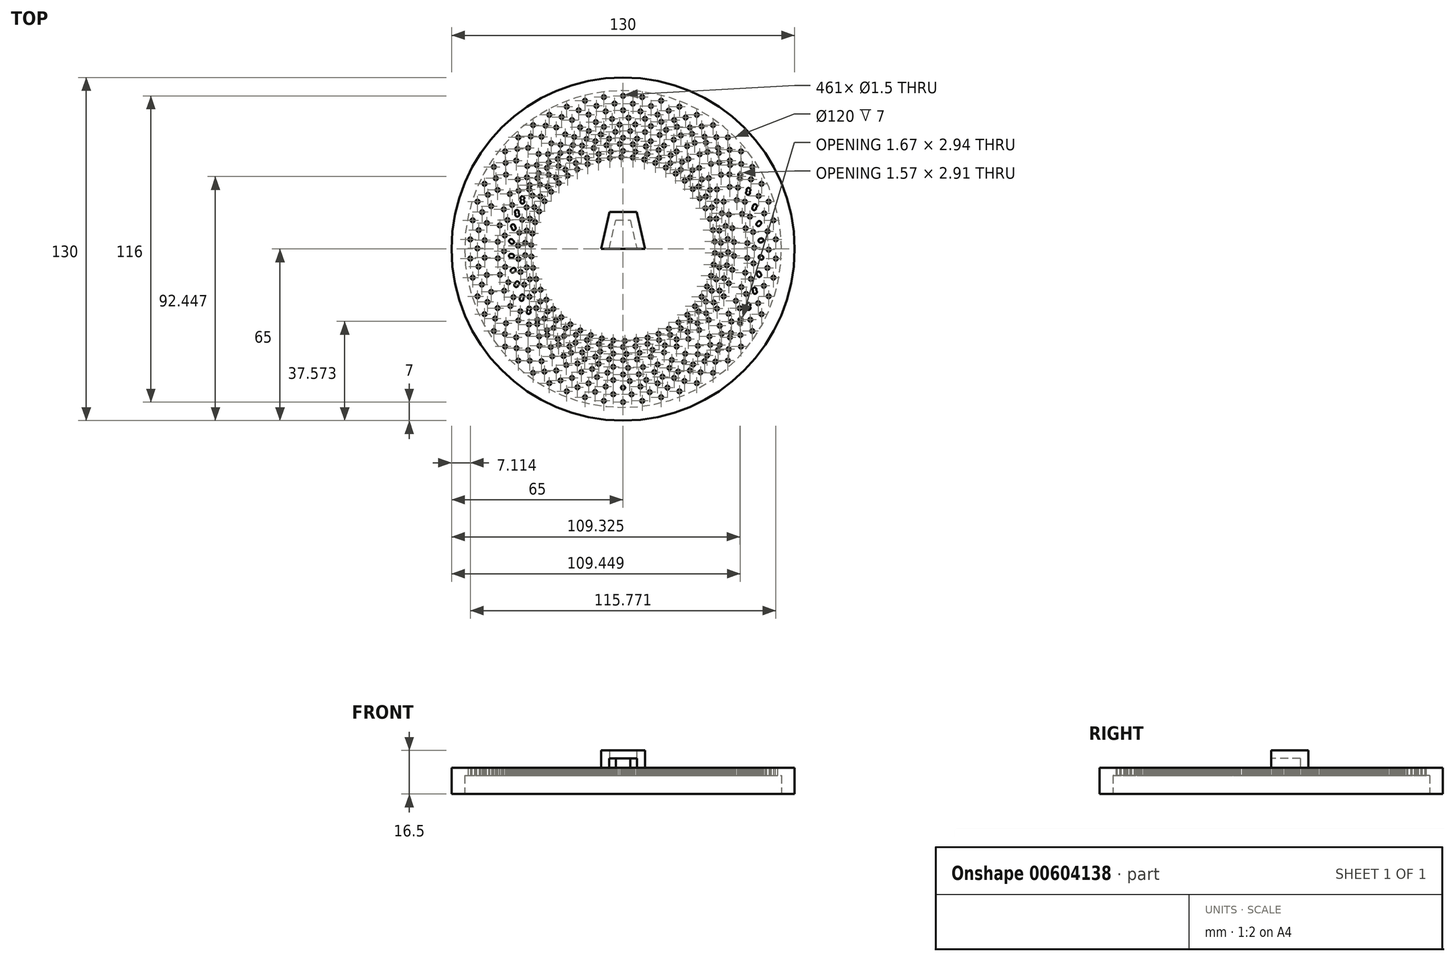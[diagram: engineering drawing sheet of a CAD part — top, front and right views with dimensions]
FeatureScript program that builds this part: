
annotation { "Feature Type Name" : "Feature", "Feature Type Description" : "" }
export const myFeature = defineFeature(function(context is Context, id is Id, definition is map)
    precondition{}
    {
        {
            var Q0;
            Q0=qCreatedBy(makeId("Top.planeOp"),FACE);
            var sketch = newSketch(context, id + "F0", { "sketchPlane" : qUnion([Q0])});
            skCircle(sketch, "E0", {"center": v(0, 0) * mm, "radius": 65 * mm});
            skSolve(sketch);
        }
        {
            var Q0;
            Q0 = qSketchRegion(id + "F0", true);
            extrude(context, id + "F1", {"entities" : qUnion([Q0]), "depth" : 10 * mm, "offsetDistance" : 25 * mm});
        }
        {
            var Q0;
            Q0=makeQuery(id+"F1.opExtrude","CAP_FACE",FACE,{"disambiguationData":[OSD([sQuery(id+"F0.wireOp",EDGE,"E0")])],"isStart":true});
            var sketch = newSketch(context, id + "F2", { "sketchPlane" : qUnion([Q0])});
            skCircle(sketch, "E1", {"center": v(0, 0) * mm, "radius": 60 * mm});
            skSolve(sketch);
        }
        {
            var Q0;
            Q0 = qSketchRegion(id + "F2", true);
            extrude(context, id + "F3", {"entities" : qUnion([Q0]), "operationType" : NewBodyOperationType.REMOVE, "oppositeDirection" : true, "depth" : 7 * mm, "offsetDistance" : 25 * mm});
        }
        {
            var Q0;
            Q0=makeQuery(id+"F1.opExtrude","CAP_FACE",FACE,{"disambiguationData":[OSD([sQuery(id+"F0.wireOp",EDGE,"E0")])],"isStart":false});
            var sketch = newSketch(context, id + "F4", { "sketchPlane" : qUnion([Q0])});
            skLineSegment(sketch, "E2", {"start": v(-5.25, 0) * mm, "end": v(-2.75, 11) * mm});
            skLineSegment(sketch, "E3", {"start": v(-2.75, 11) * mm, "end": v(2.75, 11) * mm});
            skLineSegment(sketch, "E4", {"start": v(2.75, 11) * mm, "end": v(5.25, 0) * mm});
            skPoint(sketch, "E5.end.orphan", {"position": v(0, 0) * mm});
            skPoint(sketch, "E5.start.orphan", {"position": v(0, 11) * mm});
            skLineSegment(sketch, "E6", {"start": v(-5.14, 14) * mm, "end": v(5.14, 14) * mm});
            skLineSegment(sketch, "E7", {"start": v(5.14, 14) * mm, "end": v(8.33, 0) * mm});
            skLineSegment(sketch, "E8", {"start": v(8.33, 0) * mm, "end": v(5.25, 0) * mm});
            skLineSegment(sketch, "E9", {"start": v(-5.14, 14) * mm, "end": v(-8.33, 0) * mm});
            skLineSegment(sketch, "E10", {"start": v(-8.33, 0) * mm, "end": v(-5.25, 0) * mm});
            skSolve(sketch);
        }
        {
            var Q0;
            Q0 = qSketchRegion(id + "F4", true);
            extrude(context, id + "F5", {"entities" : qUnion([Q0]), "operationType" : NewBodyOperationType.ADD, "depth" : 3.5 * mm, "offsetDistance" : 25 * mm});
        }
        {
            var Q0;
            Q0=makeQuery(id+"F5.opExtrude","CAP_FACE",FACE,{"disambiguationData":[OSD([sQuery(id+"F4.wireOp",EDGE,"E2"),sQuery(id+"F4.wireOp",EDGE,"E3"),sQuery(id+"F4.wireOp",EDGE,"E4"),sQuery(id+"F4.wireOp",EDGE,"E6"),sQuery(id+"F4.wireOp",EDGE,"E7"),sQuery(id+"F4.wireOp",EDGE,"E8"),sQuery(id+"F4.wireOp",EDGE,"E9"),sQuery(id+"F4.wireOp",EDGE,"E10")])],"isStart":false});
            var sketch = newSketch(context, id + "F6", { "sketchPlane" : qUnion([Q0])});
            skLineSegment(sketch, "E11", {"start": v(-5.14, 14) * mm, "end": v(5.14, 14) * mm});
            skLineSegment(sketch, "E12", {"start": v(5.14, 14) * mm, "end": v(8.33, 0) * mm});
            skLineSegment(sketch, "E13", {"start": v(8.33, 0) * mm, "end": v(-8.33, 0) * mm});
            skLineSegment(sketch, "E14", {"start": v(-8.33, 0) * mm, "end": v(-5.14, 14) * mm});
            skSolve(sketch);
        }
        {
            var Q0;
            Q0 = qSketchRegion(id + "F6", true);
            extrude(context, id + "F7", {"entities" : qUnion([Q0]), "operationType" : NewBodyOperationType.ADD, "depth" : 3 * mm, "offsetDistance" : 25 * mm});
        }
        {
            var Q0;
            Q0=makeQuery(id+"F1.opExtrude","CAP_FACE",FACE,{"disambiguationData":[OSD([sQuery(id+"F0.wireOp",EDGE,"E0")])],"isStart":false});
            var sketch = newSketch(context, id + "F8", { "sketchPlane" : qUnion([Q0])});
            skCircle(sketch, "E15", {"center": v(0, -58) * mm, "radius": 0.75 * mm});
            skCircle(sketch, "E16.1.0", {"center": v(7.27, -57.54) * mm, "radius": 0.75 * mm});
            skCircle(sketch, "E16.2.0", {"center": v(14.42, -56.18) * mm, "radius": 0.75 * mm});
            skCircle(sketch, "E16.3.0", {"center": v(21.35, -53.93) * mm, "radius": 0.75 * mm});
            skCircle(sketch, "E16.4.0", {"center": v(27.94, -50.83) * mm, "radius": 0.75 * mm});
            skCircle(sketch, "E16.5.0", {"center": v(34.1, -46.92) * mm, "radius": 0.75 * mm});
            skCircle(sketch, "E16.6.0", {"center": v(39.7, -42.28) * mm, "radius": 0.75 * mm});
            skCircle(sketch, "E16.7.0", {"center": v(44.69, -36.97) * mm, "radius": 0.75 * mm});
            skCircle(sketch, "E16.8.0", {"center": v(48.97, -31.08) * mm, "radius": 0.75 * mm});
            skCircle(sketch, "E16.9.0", {"center": v(52.48, -24.7) * mm, "radius": 0.75 * mm});
            skCircle(sketch, "E16.10.0", {"center": v(55.16, -17.92) * mm, "radius": 0.75 * mm});
            skCircle(sketch, "E16.11.0", {"center": v(56.97, -10.87) * mm, "radius": 0.75 * mm});
            skCircle(sketch, "E16.12.0", {"center": v(57.89, -3.64) * mm, "radius": 0.75 * mm});
            skCircle(sketch, "E16.13.0", {"center": v(57.89, 3.64) * mm, "radius": 0.75 * mm});
            skCircle(sketch, "E16.14.0", {"center": v(56.97, 10.87) * mm, "radius": 0.75 * mm});
            skCircle(sketch, "E16.15.0", {"center": v(55.16, 17.92) * mm, "radius": 0.75 * mm});
            skCircle(sketch, "E16.16.0", {"center": v(52.48, 24.7) * mm, "radius": 0.75 * mm});
            skCircle(sketch, "E16.17.0", {"center": v(48.97, 31.08) * mm, "radius": 0.75 * mm});
            skCircle(sketch, "E16.18.0", {"center": v(44.69, 36.97) * mm, "radius": 0.75 * mm});
            skCircle(sketch, "E16.19.0", {"center": v(39.7, 42.28) * mm, "radius": 0.75 * mm});
            skCircle(sketch, "E16.20.0", {"center": v(34.1, 46.92) * mm, "radius": 0.75 * mm});
            skCircle(sketch, "E16.21.0", {"center": v(27.94, 50.83) * mm, "radius": 0.75 * mm});
            skCircle(sketch, "E16.22.0", {"center": v(21.35, 53.93) * mm, "radius": 0.75 * mm});
            skCircle(sketch, "E16.23.0", {"center": v(14.42, 56.18) * mm, "radius": 0.75 * mm});
            skCircle(sketch, "E16.24.0", {"center": v(7.27, 57.54) * mm, "radius": 0.75 * mm});
            skCircle(sketch, "E16.25.0", {"center": v(0, 58) * mm, "radius": 0.75 * mm});
            skCircle(sketch, "E16.26.0", {"center": v(-7.27, 57.54) * mm, "radius": 0.75 * mm});
            skCircle(sketch, "E16.27.0", {"center": v(-14.42, 56.18) * mm, "radius": 0.75 * mm});
            skCircle(sketch, "E16.28.0", {"center": v(-21.35, 53.93) * mm, "radius": 0.75 * mm});
            skCircle(sketch, "E16.29.0", {"center": v(-27.94, 50.83) * mm, "radius": 0.75 * mm});
            skCircle(sketch, "E16.30.0", {"center": v(-34.1, 46.92) * mm, "radius": 0.75 * mm});
            skCircle(sketch, "E16.31.0", {"center": v(-39.7, 42.28) * mm, "radius": 0.75 * mm});
            skCircle(sketch, "E16.32.0", {"center": v(-44.69, 36.97) * mm, "radius": 0.75 * mm});
            skCircle(sketch, "E16.33.0", {"center": v(-48.97, 31.08) * mm, "radius": 0.75 * mm});
            skCircle(sketch, "E16.34.0", {"center": v(-52.48, 24.7) * mm, "radius": 0.75 * mm});
            skCircle(sketch, "E16.35.0", {"center": v(-55.16, 17.92) * mm, "radius": 0.75 * mm});
            skCircle(sketch, "E16.36.0", {"center": v(-56.97, 10.87) * mm, "radius": 0.75 * mm});
            skCircle(sketch, "E16.37.0", {"center": v(-57.89, 3.64) * mm, "radius": 0.75 * mm});
            skCircle(sketch, "E16.38.0", {"center": v(-57.89, -3.64) * mm, "radius": 0.75 * mm});
            skCircle(sketch, "E16.39.0", {"center": v(-56.97, -10.87) * mm, "radius": 0.75 * mm});
            skCircle(sketch, "E16.40.0", {"center": v(-55.16, -17.92) * mm, "radius": 0.75 * mm});
            skCircle(sketch, "E16.41.0", {"center": v(-52.48, -24.7) * mm, "radius": 0.75 * mm});
            skCircle(sketch, "E16.42.0", {"center": v(-48.97, -31.08) * mm, "radius": 0.75 * mm});
            skCircle(sketch, "E16.43.0", {"center": v(-44.69, -36.97) * mm, "radius": 0.75 * mm});
            skCircle(sketch, "E16.44.0", {"center": v(-39.7, -42.28) * mm, "radius": 0.75 * mm});
            skCircle(sketch, "E16.45.0", {"center": v(-34.1, -46.92) * mm, "radius": 0.75 * mm});
            skCircle(sketch, "E16.46.0", {"center": v(-27.94, -50.83) * mm, "radius": 0.75 * mm});
            skCircle(sketch, "E16.47.0", {"center": v(-21.35, -53.93) * mm, "radius": 0.75 * mm});
            skCircle(sketch, "E16.48.0", {"center": v(-14.42, -56.18) * mm, "radius": 0.75 * mm});
            skCircle(sketch, "E16.49.0", {"center": v(-7.27, -57.54) * mm, "radius": 0.75 * mm});
            skPoint(sketch, "E16.center", {"position": v(0, 0) * mm});
            skCircle(sketch, "E17", {"center": v(-3.71, -55.04) * mm, "radius": 0.75 * mm});
            skCircle(sketch, "E18.1.0", {"center": v(3.22, -55.07) * mm, "radius": 0.75 * mm});
            skCircle(sketch, "E18.2.0", {"center": v(10.1, -54.24) * mm, "radius": 0.75 * mm});
            skCircle(sketch, "E18.3.0", {"center": v(16.81, -52.54) * mm, "radius": 0.75 * mm});
            skCircle(sketch, "E18.4.0", {"center": v(23.26, -50.02) * mm, "radius": 0.75 * mm});
            skCircle(sketch, "E18.5.0", {"center": v(29.35, -46.71) * mm, "radius": 0.75 * mm});
            skCircle(sketch, "E18.6.0", {"center": v(34.97, -42.67) * mm, "radius": 0.75 * mm});
            skCircle(sketch, "E18.7.0", {"center": v(40.04, -37.95) * mm, "radius": 0.75 * mm});
            skCircle(sketch, "E18.8.0", {"center": v(44.49, -32.63) * mm, "radius": 0.75 * mm});
            skCircle(sketch, "E18.9.0", {"center": v(48.22, -26.8) * mm, "radius": 0.75 * mm});
            skCircle(sketch, "E18.10.0", {"center": v(51.2, -20.54) * mm, "radius": 0.75 * mm});
            skCircle(sketch, "E18.11.0", {"center": v(53.37, -13.96) * mm, "radius": 0.75 * mm});
            skCircle(sketch, "E18.12.0", {"center": v(54.7, -7.16) * mm, "radius": 0.75 * mm});
            skCircle(sketch, "E18.13.0", {"center": v(55.17, -0.25) * mm, "radius": 0.75 * mm});
            skCircle(sketch, "E18.14.0", {"center": v(54.76, 6.67) * mm, "radius": 0.75 * mm});
            skCircle(sketch, "E18.15.0", {"center": v(53.5, 13.48) * mm, "radius": 0.75 * mm});
            skCircle(sketch, "E18.16.0", {"center": v(51.38, 20.08) * mm, "radius": 0.75 * mm});
            skCircle(sketch, "E18.17.0", {"center": v(48.46, 26.36) * mm, "radius": 0.75 * mm});
            skCircle(sketch, "E18.18.0", {"center": v(44.78, 32.23) * mm, "radius": 0.75 * mm});
            skCircle(sketch, "E18.19.0", {"center": v(40.39, 37.58) * mm, "radius": 0.75 * mm});
            skCircle(sketch, "E18.20.0", {"center": v(35.36, 42.35) * mm, "radius": 0.75 * mm});
            skCircle(sketch, "E18.21.0", {"center": v(29.77, 46.45) * mm, "radius": 0.75 * mm});
            skCircle(sketch, "E18.22.0", {"center": v(23.71, 49.81) * mm, "radius": 0.75 * mm});
            skCircle(sketch, "E18.23.0", {"center": v(17.28, 52.4) * mm, "radius": 0.75 * mm});
            skCircle(sketch, "E18.24.0", {"center": v(10.58, 54.14) * mm, "radius": 0.75 * mm});
            skCircle(sketch, "E18.25.0", {"center": v(3.71, 55.04) * mm, "radius": 0.75 * mm});
            skCircle(sketch, "E18.26.0", {"center": v(-3.22, 55.07) * mm, "radius": 0.75 * mm});
            skCircle(sketch, "E18.27.0", {"center": v(-10.1, 54.24) * mm, "radius": 0.75 * mm});
            skCircle(sketch, "E18.28.0", {"center": v(-16.81, 52.54) * mm, "radius": 0.75 * mm});
            skCircle(sketch, "E18.29.0", {"center": v(-23.26, 50.02) * mm, "radius": 0.75 * mm});
            skCircle(sketch, "E18.30.0", {"center": v(-29.35, 46.71) * mm, "radius": 0.75 * mm});
            skCircle(sketch, "E18.31.0", {"center": v(-34.97, 42.67) * mm, "radius": 0.75 * mm});
            skCircle(sketch, "E18.32.0", {"center": v(-40.04, 37.95) * mm, "radius": 0.75 * mm});
            skCircle(sketch, "E18.33.0", {"center": v(-44.49, 32.63) * mm, "radius": 0.75 * mm});
            skCircle(sketch, "E18.34.0", {"center": v(-48.22, 26.8) * mm, "radius": 0.75 * mm});
            skCircle(sketch, "E18.35.0", {"center": v(-51.2, 20.54) * mm, "radius": 0.75 * mm});
            skCircle(sketch, "E18.36.0", {"center": v(-53.37, 13.96) * mm, "radius": 0.75 * mm});
            skCircle(sketch, "E18.37.0", {"center": v(-54.7, 7.16) * mm, "radius": 0.75 * mm});
            skCircle(sketch, "E18.38.0", {"center": v(-55.17, 0.25) * mm, "radius": 0.75 * mm});
            skCircle(sketch, "E18.39.0", {"center": v(-54.76, -6.67) * mm, "radius": 0.75 * mm});
            skCircle(sketch, "E18.40.0", {"center": v(-53.5, -13.48) * mm, "radius": 0.75 * mm});
            skCircle(sketch, "E18.41.0", {"center": v(-51.38, -20.08) * mm, "radius": 0.75 * mm});
            skCircle(sketch, "E18.42.0", {"center": v(-48.46, -26.36) * mm, "radius": 0.75 * mm});
            skCircle(sketch, "E18.43.0", {"center": v(-44.78, -32.23) * mm, "radius": 0.75 * mm});
            skCircle(sketch, "E18.44.0", {"center": v(-40.39, -37.58) * mm, "radius": 0.75 * mm});
            skCircle(sketch, "E18.45.0", {"center": v(-35.36, -42.35) * mm, "radius": 0.75 * mm});
            skCircle(sketch, "E18.46.0", {"center": v(-29.77, -46.45) * mm, "radius": 0.75 * mm});
            skCircle(sketch, "E18.47.0", {"center": v(-23.71, -49.81) * mm, "radius": 0.75 * mm});
            skCircle(sketch, "E18.48.0", {"center": v(-17.28, -52.4) * mm, "radius": 0.75 * mm});
            skCircle(sketch, "E18.49.0", {"center": v(-10.58, -54.14) * mm, "radius": 0.75 * mm});
            skCircle(sketch, "E19", {"center": v(0, -52.54) * mm, "radius": 0.75 * mm});
            skCircle(sketch, "E20.1.0", {"center": v(6.59, -52.13) * mm, "radius": 0.75 * mm});
            skCircle(sketch, "E20.2.0", {"center": v(13.07, -50.9) * mm, "radius": 0.75 * mm});
            skCircle(sketch, "E20.3.0", {"center": v(19.34, -48.85) * mm, "radius": 0.75 * mm});
            skCircle(sketch, "E20.4.0", {"center": v(25.31, -46.04) * mm, "radius": 0.75 * mm});
            skCircle(sketch, "E20.5.0", {"center": v(30.88, -42.5) * mm, "radius": 0.75 * mm});
            skCircle(sketch, "E20.6.0", {"center": v(35.97, -38.3) * mm, "radius": 0.75 * mm});
            skCircle(sketch, "E20.7.0", {"center": v(40.48, -33.5) * mm, "radius": 0.75 * mm});
            skCircle(sketch, "E20.8.0", {"center": v(44.36, -28.15) * mm, "radius": 0.75 * mm});
            skCircle(sketch, "E20.9.0", {"center": v(47.54, -22.37) * mm, "radius": 0.75 * mm});
            skCircle(sketch, "E20.10.0", {"center": v(49.97, -16.24) * mm, "radius": 0.75 * mm});
            skCircle(sketch, "E20.11.0", {"center": v(51.61, -9.85) * mm, "radius": 0.75 * mm});
            skCircle(sketch, "E20.12.0", {"center": v(52.44, -3.3) * mm, "radius": 0.75 * mm});
            skCircle(sketch, "E20.13.0", {"center": v(52.44, 3.3) * mm, "radius": 0.75 * mm});
            skCircle(sketch, "E20.14.0", {"center": v(51.61, 9.85) * mm, "radius": 0.75 * mm});
            skCircle(sketch, "E20.15.0", {"center": v(49.97, 16.24) * mm, "radius": 0.75 * mm});
            skCircle(sketch, "E20.16.0", {"center": v(47.54, 22.37) * mm, "radius": 0.75 * mm});
            skCircle(sketch, "E20.17.0", {"center": v(44.36, 28.15) * mm, "radius": 0.75 * mm});
            skCircle(sketch, "E20.18.0", {"center": v(40.48, 33.5) * mm, "radius": 0.75 * mm});
            skCircle(sketch, "E20.19.0", {"center": v(35.97, 38.3) * mm, "radius": 0.75 * mm});
            skCircle(sketch, "E20.20.0", {"center": v(30.88, 42.5) * mm, "radius": 0.75 * mm});
            skCircle(sketch, "E20.21.0", {"center": v(25.31, 46.04) * mm, "radius": 0.75 * mm});
            skCircle(sketch, "E20.22.0", {"center": v(19.34, 48.85) * mm, "radius": 0.75 * mm});
            skCircle(sketch, "E20.23.0", {"center": v(13.07, 50.9) * mm, "radius": 0.75 * mm});
            skCircle(sketch, "E20.24.0", {"center": v(6.59, 52.13) * mm, "radius": 0.75 * mm});
            skCircle(sketch, "E20.25.0", {"center": v(0, 52.54) * mm, "radius": 0.75 * mm});
            skCircle(sketch, "E20.26.0", {"center": v(-6.59, 52.13) * mm, "radius": 0.75 * mm});
            skCircle(sketch, "E20.27.0", {"center": v(-13.07, 50.9) * mm, "radius": 0.75 * mm});
            skCircle(sketch, "E20.28.0", {"center": v(-19.34, 48.85) * mm, "radius": 0.75 * mm});
            skCircle(sketch, "E20.29.0", {"center": v(-25.31, 46.04) * mm, "radius": 0.75 * mm});
            skCircle(sketch, "E20.30.0", {"center": v(-30.88, 42.5) * mm, "radius": 0.75 * mm});
            skCircle(sketch, "E20.31.0", {"center": v(-35.97, 38.3) * mm, "radius": 0.75 * mm});
            skCircle(sketch, "E20.32.0", {"center": v(-40.48, 33.5) * mm, "radius": 0.75 * mm});
            skCircle(sketch, "E20.33.0", {"center": v(-44.36, 28.15) * mm, "radius": 0.75 * mm});
            skCircle(sketch, "E20.34.0", {"center": v(-47.54, 22.37) * mm, "radius": 0.75 * mm});
            skCircle(sketch, "E20.35.0", {"center": v(-49.97, 16.24) * mm, "radius": 0.75 * mm});
            skCircle(sketch, "E20.36.0", {"center": v(-51.61, 9.85) * mm, "radius": 0.75 * mm});
            skCircle(sketch, "E20.37.0", {"center": v(-52.44, 3.3) * mm, "radius": 0.75 * mm});
            skCircle(sketch, "E20.38.0", {"center": v(-52.44, -3.3) * mm, "radius": 0.75 * mm});
            skCircle(sketch, "E20.39.0", {"center": v(-51.61, -9.85) * mm, "radius": 0.75 * mm});
            skCircle(sketch, "E20.40.0", {"center": v(-49.97, -16.24) * mm, "radius": 0.75 * mm});
            skCircle(sketch, "E20.41.0", {"center": v(-47.54, -22.37) * mm, "radius": 0.75 * mm});
            skCircle(sketch, "E20.42.0", {"center": v(-44.36, -28.15) * mm, "radius": 0.75 * mm});
            skCircle(sketch, "E20.43.0", {"center": v(-40.48, -33.5) * mm, "radius": 0.75 * mm});
            skCircle(sketch, "E20.44.0", {"center": v(-35.97, -38.3) * mm, "radius": 0.75 * mm});
            skCircle(sketch, "E20.45.0", {"center": v(-30.88, -42.5) * mm, "radius": 0.75 * mm});
            skCircle(sketch, "E20.46.0", {"center": v(-25.31, -46.04) * mm, "radius": 0.75 * mm});
            skCircle(sketch, "E20.47.0", {"center": v(-19.34, -48.85) * mm, "radius": 0.75 * mm});
            skCircle(sketch, "E20.48.0", {"center": v(-13.07, -50.9) * mm, "radius": 0.75 * mm});
            skCircle(sketch, "E20.49.0", {"center": v(-6.59, -52.13) * mm, "radius": 0.75 * mm});
            skSolve(sketch);
        }
        {
            var Q0;
            Q0 = qSketchRegion(id + "F8", true);
            extrude(context, id + "F9", {"entities" : qUnion([Q0]), "operationType" : NewBodyOperationType.REMOVE, "oppositeDirection" : true, "depth" : 25 * mm, "offsetDistance" : 25 * mm});
        }
        {
            var Q0;
            Q0=makeQuery(id+"F1.opExtrude","CAP_FACE",FACE,{"disambiguationData":[OSD([sQuery(id+"F0.wireOp",EDGE,"E0")])],"isStart":false});
            var sketch = newSketch(context, id + "F10", { "sketchPlane" : qUnion([Q0])});
            skCircle(sketch, "E21", {"center": v(-3.71, -55.04) * mm, "radius": 0.72 * mm});
            skCircle(sketch, "E22", {"center": v(-3.71, -49.68) * mm, "radius": 0.75 * mm});
            skCircle(sketch, "E23", {"center": v(0, -52.54) * mm, "radius": 0.78 * mm});
            skCircle(sketch, "E24", {"center": v(0, -47.54) * mm, "radius": 0.75 * mm});
            skCircle(sketch, "E25", {"center": v(-3.71, -44.64) * mm, "radius": 0.75 * mm});
            skCircle(sketch, "E26.1.0", {"center": v(1.9, -45.04) * mm, "radius": 0.75 * mm});
            skCircle(sketch, "E26.1.1", {"center": v(5.95, -47.46) * mm, "radius": 0.75 * mm});
            skCircle(sketch, "E26.1.2", {"center": v(2.54, -50.04) * mm, "radius": 0.75 * mm});
            skCircle(sketch, "E26.2.0", {"center": v(7.53, -44.74) * mm, "radius": 0.75 * mm});
            skCircle(sketch, "E26.2.1", {"center": v(11.85, -46.63) * mm, "radius": 0.75 * mm});
            skCircle(sketch, "E26.2.2", {"center": v(8.79, -49.62) * mm, "radius": 0.75 * mm});
            skCircle(sketch, "E26.3.0", {"center": v(13.08, -43.73) * mm, "radius": 0.75 * mm});
            skCircle(sketch, "E26.3.1", {"center": v(17.6, -45.07) * mm, "radius": 0.75 * mm});
            skCircle(sketch, "E26.3.2", {"center": v(14.93, -48.42) * mm, "radius": 0.75 * mm});
            skCircle(sketch, "E26.4.0", {"center": v(18.45, -42.04) * mm, "radius": 0.75 * mm});
            skCircle(sketch, "E26.4.1", {"center": v(23.1, -42.8) * mm, "radius": 0.75 * mm});
            skCircle(sketch, "E26.4.2", {"center": v(20.88, -46.46) * mm, "radius": 0.75 * mm});
            skCircle(sketch, "E26.5.0", {"center": v(23.57, -39.69) * mm, "radius": 0.75 * mm});
            skCircle(sketch, "E26.5.1", {"center": v(28.28, -39.85) * mm, "radius": 0.75 * mm});
            skCircle(sketch, "E26.5.2", {"center": v(26.53, -43.76) * mm, "radius": 0.75 * mm});
            skCircle(sketch, "E26.6.0", {"center": v(28.36, -36.7) * mm, "radius": 0.75 * mm});
            skCircle(sketch, "E26.6.1", {"center": v(33.05, -36.28) * mm, "radius": 0.75 * mm});
            skCircle(sketch, "E26.6.2", {"center": v(31.8, -40.38) * mm, "radius": 0.75 * mm});
            skCircle(sketch, "E26.7.0", {"center": v(32.73, -33.16) * mm, "radius": 0.75 * mm});
            skCircle(sketch, "E26.7.1", {"center": v(37.33, -32.15) * mm, "radius": 0.75 * mm});
            skCircle(sketch, "E26.7.2", {"center": v(36.61, -36.37) * mm, "radius": 0.75 * mm});
            skCircle(sketch, "E26.8.0", {"center": v(36.62, -29.08) * mm, "radius": 0.75 * mm});
            skCircle(sketch, "E26.8.1", {"center": v(41.06, -27.5) * mm, "radius": 0.75 * mm});
            skCircle(sketch, "E26.8.2", {"center": v(40.88, -31.78) * mm, "radius": 0.75 * mm});
            skCircle(sketch, "E26.9.0", {"center": v(39.98, -24.55) * mm, "radius": 0.75 * mm});
            skCircle(sketch, "E26.9.1", {"center": v(44.18, -22.43) * mm, "radius": 0.75 * mm});
            skCircle(sketch, "E26.9.2", {"center": v(44.54, -26.7) * mm, "radius": 0.75 * mm});
            skCircle(sketch, "E26.10.0", {"center": v(42.73, -19.64) * mm, "radius": 0.75 * mm});
            skCircle(sketch, "E26.10.1", {"center": v(46.64, -17) * mm, "radius": 0.75 * mm});
            skCircle(sketch, "E26.10.2", {"center": v(47.53, -21.2) * mm, "radius": 0.75 * mm});
            skCircle(sketch, "E26.11.0", {"center": v(44.85, -14.42) * mm, "radius": 0.75 * mm});
            skCircle(sketch, "E26.11.1", {"center": v(48.4, -11.32) * mm, "radius": 0.75 * mm});
            skCircle(sketch, "E26.11.2", {"center": v(49.8, -15.36) * mm, "radius": 0.75 * mm});
            skCircle(sketch, "E26.12.0", {"center": v(46.3, -8.98) * mm, "radius": 0.75 * mm});
            skCircle(sketch, "E26.12.1", {"center": v(49.44, -5.45) * mm, "radius": 0.75 * mm});
            skCircle(sketch, "E26.12.2", {"center": v(51.33, -9.3) * mm, "radius": 0.75 * mm});
            skCircle(sketch, "E26.13.0", {"center": v(47.06, -3.4) * mm, "radius": 0.75 * mm});
            skCircle(sketch, "E26.13.1", {"center": v(49.72, 0.5) * mm, "radius": 0.75 * mm});
            skCircle(sketch, "E26.13.2", {"center": v(52.09, -3.08) * mm, "radius": 0.75 * mm});
            skCircle(sketch, "E26.14.0", {"center": v(47.1, 2.24) * mm, "radius": 0.75 * mm});
            skCircle(sketch, "E26.14.1", {"center": v(49.27, 6.43) * mm, "radius": 0.75 * mm});
            skCircle(sketch, "E26.14.2", {"center": v(52.06, 3.19) * mm, "radius": 0.75 * mm});
            skCircle(sketch, "E26.15.0", {"center": v(46.45, 7.84) * mm, "radius": 0.75 * mm});
            skCircle(sketch, "E26.15.1", {"center": v(48.07, 12.27) * mm, "radius": 0.75 * mm});
            skCircle(sketch, "E26.15.2", {"center": v(51.25, 9.4) * mm, "radius": 0.75 * mm});
            skCircle(sketch, "E26.16.0", {"center": v(45.1, 13.3) * mm, "radius": 0.75 * mm});
            skCircle(sketch, "E26.16.1", {"center": v(46.15, 17.9) * mm, "radius": 0.75 * mm});
            skCircle(sketch, "E26.16.2", {"center": v(49.66, 15.45) * mm, "radius": 0.75 * mm});
            skCircle(sketch, "E26.17.0", {"center": v(43.07, 18.57) * mm, "radius": 0.75 * mm});
            skCircle(sketch, "E26.17.1", {"center": v(43.54, 23.26) * mm, "radius": 0.75 * mm});
            skCircle(sketch, "E26.17.2", {"center": v(47.33, 21.27) * mm, "radius": 0.75 * mm});
            skCircle(sketch, "E26.18.0", {"center": v(40.4, 23.53) * mm, "radius": 0.75 * mm});
            skCircle(sketch, "E26.18.1", {"center": v(40.27, 28.24) * mm, "radius": 0.75 * mm});
            skCircle(sketch, "E26.18.2", {"center": v(44.29, 26.74) * mm, "radius": 0.75 * mm});
            skCircle(sketch, "E26.19.0", {"center": v(37.13, 28.12) * mm, "radius": 0.75 * mm});
            skCircle(sketch, "E26.19.1", {"center": v(36.41, 32.77) * mm, "radius": 0.75 * mm});
            skCircle(sketch, "E26.19.2", {"center": v(40.58, 31.79) * mm, "radius": 0.75 * mm});
            skCircle(sketch, "E26.20.0", {"center": v(33.31, 32.26) * mm, "radius": 0.75 * mm});
            skCircle(sketch, "E26.20.1", {"center": v(32.01, 36.79) * mm, "radius": 0.75 * mm});
            skCircle(sketch, "E26.20.2", {"center": v(36.27, 36.33) * mm, "radius": 0.75 * mm});
            skCircle(sketch, "E26.21.0", {"center": v(29, 35.89) * mm, "radius": 0.75 * mm});
            skCircle(sketch, "E26.21.1", {"center": v(27.15, 40.22) * mm, "radius": 0.75 * mm});
            skCircle(sketch, "E26.21.2", {"center": v(31.43, 40.3) * mm, "radius": 0.75 * mm});
            skCircle(sketch, "E26.22.0", {"center": v(24.27, 38.95) * mm, "radius": 0.75 * mm});
            skCircle(sketch, "E26.22.1", {"center": v(21.89, 43.01) * mm, "radius": 0.75 * mm});
            skCircle(sketch, "E26.22.2", {"center": v(26.13, 43.63) * mm, "radius": 0.75 * mm});
            skCircle(sketch, "E26.23.0", {"center": v(19.2, 41.4) * mm, "radius": 0.75 * mm});
            skCircle(sketch, "E26.23.1", {"center": v(16.32, 45.13) * mm, "radius": 0.75 * mm});
            skCircle(sketch, "E26.23.2", {"center": v(20.45, 46.27) * mm, "radius": 0.75 * mm});
            skCircle(sketch, "E26.24.0", {"center": v(13.85, 43.18) * mm, "radius": 0.75 * mm});
            skCircle(sketch, "E26.24.1", {"center": v(10.53, 46.53) * mm, "radius": 0.75 * mm});
            skCircle(sketch, "E26.24.2", {"center": v(14.48, 48.18) * mm, "radius": 0.75 * mm});
            skCircle(sketch, "E26.25.0", {"center": v(8.33, 44.29) * mm, "radius": 0.75 * mm});
            skCircle(sketch, "E26.25.1", {"center": v(4.61, 47.2) * mm, "radius": 0.75 * mm});
            skCircle(sketch, "E26.25.2", {"center": v(8.33, 49.33) * mm, "radius": 0.75 * mm});
            skCircle(sketch, "E26.26.0", {"center": v(2.7, 44.7) * mm, "radius": 0.75 * mm});
            skCircle(sketch, "E26.26.1", {"center": v(-1.34, 47.1) * mm, "radius": 0.75 * mm});
            skCircle(sketch, "E26.26.2", {"center": v(2.07, 49.7) * mm, "radius": 0.75 * mm});
            skCircle(sketch, "E26.27.0", {"center": v(-2.92, 44.39) * mm, "radius": 0.75 * mm});
            skCircle(sketch, "E26.27.1", {"center": v(-7.24, 46.28) * mm, "radius": 0.75 * mm});
            skCircle(sketch, "E26.27.2", {"center": v(-4.17, 49.27) * mm, "radius": 0.75 * mm});
            skCircle(sketch, "E26.28.0", {"center": v(-8.46, 43.38) * mm, "radius": 0.75 * mm});
            skCircle(sketch, "E26.28.1", {"center": v(-12.98, 44.71) * mm, "radius": 0.75 * mm});
            skCircle(sketch, "E26.28.2", {"center": v(-10.32, 48.07) * mm, "radius": 0.75 * mm});
            skCircle(sketch, "E26.29.0", {"center": v(-13.84, 41.69) * mm, "radius": 0.75 * mm});
            skCircle(sketch, "E26.29.1", {"center": v(-18.5, 42.44) * mm, "radius": 0.75 * mm});
            skCircle(sketch, "E26.29.2", {"center": v(-16.27, 46.1) * mm, "radius": 0.75 * mm});
            skCircle(sketch, "E26.30.0", {"center": v(-18.96, 39.33) * mm, "radius": 0.75 * mm});
            skCircle(sketch, "E26.30.1", {"center": v(-23.67, 39.5) * mm, "radius": 0.75 * mm});
            skCircle(sketch, "E26.30.2", {"center": v(-21.92, 43.4) * mm, "radius": 0.75 * mm});
            skCircle(sketch, "E26.31.0", {"center": v(-23.74, 36.36) * mm, "radius": 0.75 * mm});
            skCircle(sketch, "E26.31.1", {"center": v(-28.44, 35.93) * mm, "radius": 0.75 * mm});
            skCircle(sketch, "E26.31.2", {"center": v(-27.2, 40.03) * mm, "radius": 0.75 * mm});
            skCircle(sketch, "E26.32.0", {"center": v(-28.12, 32.8) * mm, "radius": 0.75 * mm});
            skCircle(sketch, "E26.32.1", {"center": v(-32.72, 31.8) * mm, "radius": 0.75 * mm});
            skCircle(sketch, "E26.32.2", {"center": v(-32, 36.02) * mm, "radius": 0.75 * mm});
            skCircle(sketch, "E26.33.0", {"center": v(-32, 28.73) * mm, "radius": 0.75 * mm});
            skCircle(sketch, "E26.33.1", {"center": v(-36.45, 27.15) * mm, "radius": 0.75 * mm});
            skCircle(sketch, "E26.33.2", {"center": v(-36.26, 31.43) * mm, "radius": 0.75 * mm});
            skCircle(sketch, "E26.34.0", {"center": v(-35.36, 24.2) * mm, "radius": 0.75 * mm});
            skCircle(sketch, "E26.34.1", {"center": v(-39.57, 22.08) * mm, "radius": 0.75 * mm});
            skCircle(sketch, "E26.34.2", {"center": v(-39.92, 26.35) * mm, "radius": 0.75 * mm});
            skCircle(sketch, "E26.35.0", {"center": v(-38.12, 19.29) * mm, "radius": 0.75 * mm});
            skCircle(sketch, "E26.35.1", {"center": v(-42.03, 16.65) * mm, "radius": 0.75 * mm});
            skCircle(sketch, "E26.35.2", {"center": v(-42.91, 20.85) * mm, "radius": 0.75 * mm});
            skCircle(sketch, "E26.36.0", {"center": v(-40.24, 14.07) * mm, "radius": 0.75 * mm});
            skCircle(sketch, "E26.36.1", {"center": v(-43.79, 10.97) * mm, "radius": 0.75 * mm});
            skCircle(sketch, "E26.36.2", {"center": v(-45.2, 15.01) * mm, "radius": 0.75 * mm});
            skCircle(sketch, "E26.37.0", {"center": v(-41.69, 8.62) * mm, "radius": 0.75 * mm});
            skCircle(sketch, "E26.37.1", {"center": v(-44.82, 5.1) * mm, "radius": 0.75 * mm});
            skCircle(sketch, "E26.37.2", {"center": v(-46.72, 8.94) * mm, "radius": 0.75 * mm});
            skCircle(sketch, "E26.38.0", {"center": v(-42.45, 3.04) * mm, "radius": 0.75 * mm});
            skCircle(sketch, "E26.38.1", {"center": v(-45.11, -0.85) * mm, "radius": 0.75 * mm});
            skCircle(sketch, "E26.38.2", {"center": v(-47.48, 2.72) * mm, "radius": 0.75 * mm});
            skCircle(sketch, "E26.39.0", {"center": v(-42.5, -2.6) * mm, "radius": 0.75 * mm});
            skCircle(sketch, "E26.39.1", {"center": v(-44.65, -6.79) * mm, "radius": 0.75 * mm});
            skCircle(sketch, "E26.39.2", {"center": v(-47.45, -3.54) * mm, "radius": 0.75 * mm});
            skCircle(sketch, "E26.40.0", {"center": v(-41.84, -8.2) * mm, "radius": 0.75 * mm});
            skCircle(sketch, "E26.40.1", {"center": v(-43.45, -12.62) * mm, "radius": 0.75 * mm});
            skCircle(sketch, "E26.40.2", {"center": v(-46.63, -9.75) * mm, "radius": 0.75 * mm});
            skCircle(sketch, "E26.41.0", {"center": v(-40.49, -13.66) * mm, "radius": 0.75 * mm});
            skCircle(sketch, "E26.41.1", {"center": v(-41.53, -18.26) * mm, "radius": 0.75 * mm});
            skCircle(sketch, "E26.41.2", {"center": v(-45.05, -15.8) * mm, "radius": 0.75 * mm});
            skCircle(sketch, "E26.42.0", {"center": v(-38.46, -18.92) * mm, "radius": 0.75 * mm});
            skCircle(sketch, "E26.42.1", {"center": v(-38.92, -23.6) * mm, "radius": 0.75 * mm});
            skCircle(sketch, "E26.42.2", {"center": v(-42.71, -21.62) * mm, "radius": 0.75 * mm});
            skCircle(sketch, "E26.43.0", {"center": v(-35.79, -23.88) * mm, "radius": 0.75 * mm});
            skCircle(sketch, "E26.43.1", {"center": v(-35.66, -28.6) * mm, "radius": 0.75 * mm});
            skCircle(sketch, "E26.43.2", {"center": v(-39.67, -27.1) * mm, "radius": 0.75 * mm});
            skCircle(sketch, "E26.44.0", {"center": v(-32.52, -28.47) * mm, "radius": 0.75 * mm});
            skCircle(sketch, "E26.44.1", {"center": v(-31.8, -33.13) * mm, "radius": 0.75 * mm});
            skCircle(sketch, "E26.44.2", {"center": v(-35.97, -32.14) * mm, "radius": 0.75 * mm});
            skCircle(sketch, "E26.45.0", {"center": v(-28.7, -32.6) * mm, "radius": 0.75 * mm});
            skCircle(sketch, "E26.45.1", {"center": v(-27.4, -37.14) * mm, "radius": 0.75 * mm});
            skCircle(sketch, "E26.45.2", {"center": v(-31.66, -36.69) * mm, "radius": 0.75 * mm});
            skCircle(sketch, "E26.46.0", {"center": v(-24.39, -36.24) * mm, "radius": 0.75 * mm});
            skCircle(sketch, "E26.46.1", {"center": v(-22.53, -40.57) * mm, "radius": 0.75 * mm});
            skCircle(sketch, "E26.46.2", {"center": v(-26.82, -40.66) * mm, "radius": 0.75 * mm});
            skCircle(sketch, "E26.47.0", {"center": v(-19.66, -39.3) * mm, "radius": 0.75 * mm});
            skCircle(sketch, "E26.47.1", {"center": v(-17.27, -43.37) * mm, "radius": 0.75 * mm});
            skCircle(sketch, "E26.47.2", {"center": v(-21.51, -43.99) * mm, "radius": 0.75 * mm});
            skCircle(sketch, "E26.48.0", {"center": v(-14.58, -41.75) * mm, "radius": 0.75 * mm});
            skCircle(sketch, "E26.48.1", {"center": v(-11.7, -45.48) * mm, "radius": 0.75 * mm});
            skCircle(sketch, "E26.48.2", {"center": v(-15.83, -46.63) * mm, "radius": 0.75 * mm});
            skCircle(sketch, "E26.49.0", {"center": v(-9.24, -43.53) * mm, "radius": 0.75 * mm});
            skCircle(sketch, "E26.49.1", {"center": v(-5.92, -46.88) * mm, "radius": 0.75 * mm});
            skCircle(sketch, "E26.49.2", {"center": v(-9.87, -48.53) * mm, "radius": 0.75 * mm});
            skPoint(sketch, "E26.center", {"position": v(2.3, -0.18) * mm});
            skSolve(sketch);
        }
        {
            var Q0;
            Q0 = qSketchRegion(id + "F10", true);
            extrude(context, id + "F11", {"entities" : qUnion([Q0]), "operationType" : NewBodyOperationType.REMOVE, "oppositeDirection" : true, "depth" : 25 * mm, "offsetDistance" : 25 * mm});
        }
        {
            var Q0;
            Q0=makeQuery(id+"F1.opExtrude","CAP_FACE",FACE,{"disambiguationData":[OSD([sQuery(id+"F0.wireOp",EDGE,"E0")])],"isStart":false});
            var sketch = newSketch(context, id + "F12", { "sketchPlane" : qUnion([Q0])});
            skCircle(sketch, "E27", {"center": v(-3.71, -44.64) * mm, "radius": 0.75 * mm});
            skCircle(sketch, "E28", {"center": v(0, -47.54) * mm, "radius": 0.75 * mm});
            skCircle(sketch, "E29", {"center": v(0, -42.14) * mm, "radius": 0.75 * mm});
            skCircle(sketch, "E30", {"center": v(0, -37.14) * mm, "radius": 0.75 * mm});
            skCircle(sketch, "E31", {"center": v(-3.71, -39.64) * mm, "radius": 0.75 * mm});
            skCircle(sketch, "E32", {"center": v(-3.71, -34.64) * mm, "radius": 0.75 * mm});
            skCircle(sketch, "E33.1.0", {"center": v(1.29, -39.8) * mm, "radius": 0.75 * mm});
            skCircle(sketch, "E33.1.1", {"center": v(5.28, -41.8) * mm, "radius": 0.75 * mm});
            skCircle(sketch, "E33.1.2", {"center": v(4.65, -36.85) * mm, "radius": 0.75 * mm});
            skCircle(sketch, "E33.1.3", {"center": v(0.66, -34.83) * mm, "radius": 0.75 * mm});
            skCircle(sketch, "E33.2.0", {"center": v(6.26, -39.32) * mm, "radius": 0.75 * mm});
            skCircle(sketch, "E33.2.1", {"center": v(10.48, -40.81) * mm, "radius": 0.75 * mm});
            skCircle(sketch, "E33.2.2", {"center": v(9.24, -35.97) * mm, "radius": 0.75 * mm});
            skCircle(sketch, "E33.2.3", {"center": v(5.02, -34.47) * mm, "radius": 0.75 * mm});
            skCircle(sketch, "E33.3.0", {"center": v(11.14, -38.22) * mm, "radius": 0.75 * mm});
            skCircle(sketch, "E33.3.1", {"center": v(15.51, -39.18) * mm, "radius": 0.75 * mm});
            skCircle(sketch, "E33.3.2", {"center": v(13.67, -34.53) * mm, "radius": 0.75 * mm});
            skCircle(sketch, "E33.3.3", {"center": v(9.3, -33.57) * mm, "radius": 0.75 * mm});
            skCircle(sketch, "E33.4.0", {"center": v(15.84, -36.52) * mm, "radius": 0.75 * mm});
            skCircle(sketch, "E33.4.1", {"center": v(20.3, -36.93) * mm, "radius": 0.75 * mm});
            skCircle(sketch, "E33.4.2", {"center": v(17.9, -32.55) * mm, "radius": 0.75 * mm});
            skCircle(sketch, "E33.4.3", {"center": v(13.43, -32.14) * mm, "radius": 0.75 * mm});
            skCircle(sketch, "E33.5.0", {"center": v(20.3, -34.25) * mm, "radius": 0.75 * mm});
            skCircle(sketch, "E33.5.1", {"center": v(24.77, -34.1) * mm, "radius": 0.75 * mm});
            skCircle(sketch, "E33.5.2", {"center": v(21.83, -30.05) * mm, "radius": 0.75 * mm});
            skCircle(sketch, "E33.5.3", {"center": v(17.36, -30.2) * mm, "radius": 0.75 * mm});
            skCircle(sketch, "E33.6.0", {"center": v(24.43, -31.44) * mm, "radius": 0.75 * mm});
            skCircle(sketch, "E33.6.1", {"center": v(28.85, -30.72) * mm, "radius": 0.75 * mm});
            skCircle(sketch, "E33.6.2", {"center": v(25.42, -27.07) * mm, "radius": 0.75 * mm});
            skCircle(sketch, "E33.6.3", {"center": v(21, -27.8) * mm, "radius": 0.75 * mm});
            skCircle(sketch, "E33.7.0", {"center": v(28.18, -28.13) * mm, "radius": 0.75 * mm});
            skCircle(sketch, "E33.7.1", {"center": v(32.47, -26.86) * mm, "radius": 0.75 * mm});
            skCircle(sketch, "E33.7.2", {"center": v(28.62, -23.67) * mm, "radius": 0.75 * mm});
            skCircle(sketch, "E33.7.3", {"center": v(24.32, -24.94) * mm, "radius": 0.75 * mm});
            skCircle(sketch, "E33.8.0", {"center": v(31.48, -24.37) * mm, "radius": 0.75 * mm});
            skCircle(sketch, "E33.8.1", {"center": v(35.58, -22.58) * mm, "radius": 0.75 * mm});
            skCircle(sketch, "E33.8.2", {"center": v(31.36, -19.9) * mm, "radius": 0.75 * mm});
            skCircle(sketch, "E33.8.3", {"center": v(27.26, -21.7) * mm, "radius": 0.75 * mm});
            skCircle(sketch, "E33.9.0", {"center": v(34.29, -20.24) * mm, "radius": 0.75 * mm});
            skCircle(sketch, "E33.9.1", {"center": v(38.13, -17.94) * mm, "radius": 0.75 * mm});
            skCircle(sketch, "E33.9.2", {"center": v(33.6, -15.81) * mm, "radius": 0.75 * mm});
            skCircle(sketch, "E33.9.3", {"center": v(29.76, -18.1) * mm, "radius": 0.75 * mm});
            skCircle(sketch, "E33.10.0", {"center": v(36.55, -15.78) * mm, "radius": 0.75 * mm});
            skCircle(sketch, "E33.10.1", {"center": v(40.08, -13.02) * mm, "radius": 0.75 * mm});
            skCircle(sketch, "E33.10.2", {"center": v(35.32, -11.48) * mm, "radius": 0.75 * mm});
            skCircle(sketch, "E33.10.3", {"center": v(31.8, -14.23) * mm, "radius": 0.75 * mm});
            skCircle(sketch, "E33.11.0", {"center": v(38.24, -11.07) * mm, "radius": 0.75 * mm});
            skCircle(sketch, "E33.11.1", {"center": v(41.4, -7.9) * mm, "radius": 0.75 * mm});
            skCircle(sketch, "E33.11.2", {"center": v(36.48, -6.96) * mm, "radius": 0.75 * mm});
            skCircle(sketch, "E33.11.3", {"center": v(33.33, -10.14) * mm, "radius": 0.75 * mm});
            skCircle(sketch, "E33.12.0", {"center": v(39.33, -6.2) * mm, "radius": 0.75 * mm});
            skCircle(sketch, "E33.12.1", {"center": v(42.06, -2.65) * mm, "radius": 0.75 * mm});
            skCircle(sketch, "E33.12.2", {"center": v(37.07, -2.33) * mm, "radius": 0.75 * mm});
            skCircle(sketch, "E33.12.3", {"center": v(34.34, -5.88) * mm, "radius": 0.75 * mm});
            skCircle(sketch, "E33.13.0", {"center": v(39.8, -1.22) * mm, "radius": 0.75 * mm});
            skCircle(sketch, "E33.13.1", {"center": v(42.06, 2.65) * mm, "radius": 0.75 * mm});
            skCircle(sketch, "E33.13.2", {"center": v(37.07, 2.33) * mm, "radius": 0.75 * mm});
            skCircle(sketch, "E33.13.3", {"center": v(34.8, -1.53) * mm, "radius": 0.75 * mm});
            skCircle(sketch, "E33.14.0", {"center": v(39.63, 3.78) * mm, "radius": 0.75 * mm});
            skCircle(sketch, "E33.14.1", {"center": v(41.4, 7.9) * mm, "radius": 0.75 * mm});
            skCircle(sketch, "E33.14.2", {"center": v(36.48, 6.96) * mm, "radius": 0.75 * mm});
            skCircle(sketch, "E33.14.3", {"center": v(34.72, 2.84) * mm, "radius": 0.75 * mm});
            skCircle(sketch, "E33.15.0", {"center": v(38.85, 8.72) * mm, "radius": 0.75 * mm});
            skCircle(sketch, "E33.15.1", {"center": v(40.08, 13.02) * mm, "radius": 0.75 * mm});
            skCircle(sketch, "E33.15.2", {"center": v(35.32, 11.48) * mm, "radius": 0.75 * mm});
            skCircle(sketch, "E33.15.3", {"center": v(34.1, 7.17) * mm, "radius": 0.75 * mm});
            skCircle(sketch, "E33.16.0", {"center": v(37.45, 13.52) * mm, "radius": 0.75 * mm});
            skCircle(sketch, "E33.16.1", {"center": v(38.13, 17.94) * mm, "radius": 0.75 * mm});
            skCircle(sketch, "E33.16.2", {"center": v(33.6, 15.81) * mm, "radius": 0.75 * mm});
            skCircle(sketch, "E33.16.3", {"center": v(32.92, 11.39) * mm, "radius": 0.75 * mm});
            skCircle(sketch, "E33.17.0", {"center": v(35.46, 18.1) * mm, "radius": 0.75 * mm});
            skCircle(sketch, "E33.17.1", {"center": v(35.58, 22.58) * mm, "radius": 0.75 * mm});
            skCircle(sketch, "E33.17.2", {"center": v(31.36, 19.9) * mm, "radius": 0.75 * mm});
            skCircle(sketch, "E33.17.3", {"center": v(31.24, 15.43) * mm, "radius": 0.75 * mm});
            skCircle(sketch, "E33.18.0", {"center": v(32.9, 22.4) * mm, "radius": 0.75 * mm});
            skCircle(sketch, "E33.18.1", {"center": v(32.47, 26.86) * mm, "radius": 0.75 * mm});
            skCircle(sketch, "E33.18.2", {"center": v(28.62, 23.67) * mm, "radius": 0.75 * mm});
            skCircle(sketch, "E33.18.3", {"center": v(29.06, 19.22) * mm, "radius": 0.75 * mm});
            skCircle(sketch, "E33.19.0", {"center": v(29.84, 26.35) * mm, "radius": 0.75 * mm});
            skCircle(sketch, "E33.19.1", {"center": v(28.85, 30.72) * mm, "radius": 0.75 * mm});
            skCircle(sketch, "E33.19.2", {"center": v(25.42, 27.07) * mm, "radius": 0.75 * mm});
            skCircle(sketch, "E33.19.3", {"center": v(26.42, 22.7) * mm, "radius": 0.75 * mm});
            skCircle(sketch, "E33.20.0", {"center": v(26.3, 29.89) * mm, "radius": 0.75 * mm});
            skCircle(sketch, "E33.20.1", {"center": v(24.77, 34.1) * mm, "radius": 0.75 * mm});
            skCircle(sketch, "E33.20.2", {"center": v(21.83, 30.05) * mm, "radius": 0.75 * mm});
            skCircle(sketch, "E33.20.3", {"center": v(23.36, 25.84) * mm, "radius": 0.75 * mm});
            skCircle(sketch, "E33.21.0", {"center": v(22.35, 32.95) * mm, "radius": 0.75 * mm});
            skCircle(sketch, "E33.21.1", {"center": v(20.3, 36.93) * mm, "radius": 0.75 * mm});
            skCircle(sketch, "E33.21.2", {"center": v(17.9, 32.55) * mm, "radius": 0.75 * mm});
            skCircle(sketch, "E33.21.3", {"center": v(19.94, 28.57) * mm, "radius": 0.75 * mm});
            skCircle(sketch, "E33.22.0", {"center": v(18.04, 35.49) * mm, "radius": 0.75 * mm});
            skCircle(sketch, "E33.22.1", {"center": v(15.51, 39.18) * mm, "radius": 0.75 * mm});
            skCircle(sketch, "E33.22.2", {"center": v(13.67, 34.53) * mm, "radius": 0.75 * mm});
            skCircle(sketch, "E33.22.3", {"center": v(16.2, 30.84) * mm, "radius": 0.75 * mm});
            skCircle(sketch, "E33.23.0", {"center": v(13.45, 37.47) * mm, "radius": 0.75 * mm});
            skCircle(sketch, "E33.23.1", {"center": v(10.48, 40.81) * mm, "radius": 0.75 * mm});
            skCircle(sketch, "E33.23.2", {"center": v(9.24, 35.97) * mm, "radius": 0.75 * mm});
            skCircle(sketch, "E33.23.3", {"center": v(12.2, 32.63) * mm, "radius": 0.75 * mm});
            skCircle(sketch, "E33.24.0", {"center": v(8.65, 38.86) * mm, "radius": 0.75 * mm});
            skCircle(sketch, "E33.24.1", {"center": v(5.28, 41.8) * mm, "radius": 0.75 * mm});
            skCircle(sketch, "E33.24.2", {"center": v(4.65, 36.85) * mm, "radius": 0.75 * mm});
            skCircle(sketch, "E33.24.3", {"center": v(8.02, 33.9) * mm, "radius": 0.75 * mm});
            skCircle(sketch, "E33.25.0", {"center": v(3.71, 39.64) * mm, "radius": 0.75 * mm});
            skCircle(sketch, "E33.25.1", {"center": v(0, 42.14) * mm, "radius": 0.75 * mm});
            skCircle(sketch, "E33.25.2", {"center": v(0, 37.14) * mm, "radius": 0.75 * mm});
            skCircle(sketch, "E33.25.3", {"center": v(3.71, 34.64) * mm, "radius": 0.75 * mm});
            skCircle(sketch, "E33.26.0", {"center": v(-1.29, 39.8) * mm, "radius": 0.75 * mm});
            skCircle(sketch, "E33.26.1", {"center": v(-5.28, 41.8) * mm, "radius": 0.75 * mm});
            skCircle(sketch, "E33.26.2", {"center": v(-4.65, 36.85) * mm, "radius": 0.75 * mm});
            skCircle(sketch, "E33.26.3", {"center": v(-0.66, 34.83) * mm, "radius": 0.75 * mm});
            skCircle(sketch, "E33.27.0", {"center": v(-6.26, 39.32) * mm, "radius": 0.75 * mm});
            skCircle(sketch, "E33.27.1", {"center": v(-10.48, 40.81) * mm, "radius": 0.75 * mm});
            skCircle(sketch, "E33.27.2", {"center": v(-9.24, 35.97) * mm, "radius": 0.75 * mm});
            skCircle(sketch, "E33.27.3", {"center": v(-5.02, 34.47) * mm, "radius": 0.75 * mm});
            skCircle(sketch, "E33.28.0", {"center": v(-11.14, 38.22) * mm, "radius": 0.75 * mm});
            skCircle(sketch, "E33.28.1", {"center": v(-15.51, 39.18) * mm, "radius": 0.75 * mm});
            skCircle(sketch, "E33.28.2", {"center": v(-13.67, 34.53) * mm, "radius": 0.75 * mm});
            skCircle(sketch, "E33.28.3", {"center": v(-9.3, 33.57) * mm, "radius": 0.75 * mm});
            skCircle(sketch, "E33.29.0", {"center": v(-15.84, 36.52) * mm, "radius": 0.75 * mm});
            skCircle(sketch, "E33.29.1", {"center": v(-20.3, 36.93) * mm, "radius": 0.75 * mm});
            skCircle(sketch, "E33.29.2", {"center": v(-17.9, 32.55) * mm, "radius": 0.75 * mm});
            skCircle(sketch, "E33.29.3", {"center": v(-13.43, 32.14) * mm, "radius": 0.75 * mm});
            skCircle(sketch, "E33.30.0", {"center": v(-20.3, 34.25) * mm, "radius": 0.75 * mm});
            skCircle(sketch, "E33.30.1", {"center": v(-24.77, 34.1) * mm, "radius": 0.75 * mm});
            skCircle(sketch, "E33.30.2", {"center": v(-21.83, 30.05) * mm, "radius": 0.75 * mm});
            skCircle(sketch, "E33.30.3", {"center": v(-17.36, 30.2) * mm, "radius": 0.75 * mm});
            skCircle(sketch, "E33.31.0", {"center": v(-24.43, 31.44) * mm, "radius": 0.75 * mm});
            skCircle(sketch, "E33.31.1", {"center": v(-28.85, 30.72) * mm, "radius": 0.75 * mm});
            skCircle(sketch, "E33.31.2", {"center": v(-25.42, 27.07) * mm, "radius": 0.75 * mm});
            skCircle(sketch, "E33.31.3", {"center": v(-21, 27.8) * mm, "radius": 0.75 * mm});
            skCircle(sketch, "E33.32.0", {"center": v(-28.18, 28.13) * mm, "radius": 0.75 * mm});
            skCircle(sketch, "E33.32.1", {"center": v(-32.47, 26.86) * mm, "radius": 0.75 * mm});
            skCircle(sketch, "E33.32.2", {"center": v(-28.62, 23.67) * mm, "radius": 0.75 * mm});
            skCircle(sketch, "E33.32.3", {"center": v(-24.32, 24.94) * mm, "radius": 0.75 * mm});
            skCircle(sketch, "E33.33.0", {"center": v(-31.48, 24.37) * mm, "radius": 0.75 * mm});
            skCircle(sketch, "E33.33.1", {"center": v(-35.58, 22.58) * mm, "radius": 0.75 * mm});
            skCircle(sketch, "E33.33.2", {"center": v(-31.36, 19.9) * mm, "radius": 0.75 * mm});
            skCircle(sketch, "E33.33.3", {"center": v(-27.26, 21.7) * mm, "radius": 0.75 * mm});
            skCircle(sketch, "E33.34.0", {"center": v(-34.29, 20.24) * mm, "radius": 0.75 * mm});
            skCircle(sketch, "E33.34.1", {"center": v(-38.13, 17.94) * mm, "radius": 0.75 * mm});
            skCircle(sketch, "E33.34.2", {"center": v(-33.6, 15.81) * mm, "radius": 0.75 * mm});
            skCircle(sketch, "E33.34.3", {"center": v(-29.76, 18.1) * mm, "radius": 0.75 * mm});
            skCircle(sketch, "E33.35.0", {"center": v(-36.55, 15.78) * mm, "radius": 0.75 * mm});
            skCircle(sketch, "E33.35.1", {"center": v(-40.08, 13.02) * mm, "radius": 0.75 * mm});
            skCircle(sketch, "E33.35.2", {"center": v(-35.32, 11.48) * mm, "radius": 0.75 * mm});
            skCircle(sketch, "E33.35.3", {"center": v(-31.8, 14.23) * mm, "radius": 0.75 * mm});
            skCircle(sketch, "E33.36.0", {"center": v(-38.24, 11.07) * mm, "radius": 0.75 * mm});
            skCircle(sketch, "E33.36.1", {"center": v(-41.4, 7.9) * mm, "radius": 0.75 * mm});
            skCircle(sketch, "E33.36.2", {"center": v(-36.48, 6.96) * mm, "radius": 0.75 * mm});
            skCircle(sketch, "E33.36.3", {"center": v(-33.33, 10.14) * mm, "radius": 0.75 * mm});
            skCircle(sketch, "E33.37.0", {"center": v(-39.33, 6.2) * mm, "radius": 0.75 * mm});
            skCircle(sketch, "E33.37.1", {"center": v(-42.06, 2.65) * mm, "radius": 0.75 * mm});
            skCircle(sketch, "E33.37.2", {"center": v(-37.07, 2.33) * mm, "radius": 0.75 * mm});
            skCircle(sketch, "E33.37.3", {"center": v(-34.34, 5.88) * mm, "radius": 0.75 * mm});
            skCircle(sketch, "E33.38.0", {"center": v(-39.8, 1.22) * mm, "radius": 0.75 * mm});
            skCircle(sketch, "E33.38.1", {"center": v(-42.06, -2.65) * mm, "radius": 0.75 * mm});
            skCircle(sketch, "E33.38.2", {"center": v(-37.07, -2.33) * mm, "radius": 0.75 * mm});
            skCircle(sketch, "E33.38.3", {"center": v(-34.8, 1.53) * mm, "radius": 0.75 * mm});
            skCircle(sketch, "E33.39.0", {"center": v(-39.63, -3.78) * mm, "radius": 0.75 * mm});
            skCircle(sketch, "E33.39.1", {"center": v(-41.4, -7.9) * mm, "radius": 0.75 * mm});
            skCircle(sketch, "E33.39.2", {"center": v(-36.48, -6.96) * mm, "radius": 0.75 * mm});
            skCircle(sketch, "E33.39.3", {"center": v(-34.72, -2.84) * mm, "radius": 0.75 * mm});
            skCircle(sketch, "E33.40.0", {"center": v(-38.85, -8.72) * mm, "radius": 0.75 * mm});
            skCircle(sketch, "E33.40.1", {"center": v(-40.08, -13.02) * mm, "radius": 0.75 * mm});
            skCircle(sketch, "E33.40.2", {"center": v(-35.32, -11.48) * mm, "radius": 0.75 * mm});
            skCircle(sketch, "E33.40.3", {"center": v(-34.1, -7.17) * mm, "radius": 0.75 * mm});
            skCircle(sketch, "E33.41.0", {"center": v(-37.45, -13.52) * mm, "radius": 0.75 * mm});
            skCircle(sketch, "E33.41.1", {"center": v(-38.13, -17.94) * mm, "radius": 0.75 * mm});
            skCircle(sketch, "E33.41.2", {"center": v(-33.6, -15.81) * mm, "radius": 0.75 * mm});
            skCircle(sketch, "E33.41.3", {"center": v(-32.92, -11.39) * mm, "radius": 0.75 * mm});
            skCircle(sketch, "E33.42.0", {"center": v(-35.46, -18.1) * mm, "radius": 0.75 * mm});
            skCircle(sketch, "E33.42.1", {"center": v(-35.58, -22.58) * mm, "radius": 0.75 * mm});
            skCircle(sketch, "E33.42.2", {"center": v(-31.36, -19.9) * mm, "radius": 0.75 * mm});
            skCircle(sketch, "E33.42.3", {"center": v(-31.24, -15.43) * mm, "radius": 0.75 * mm});
            skCircle(sketch, "E33.43.0", {"center": v(-32.9, -22.4) * mm, "radius": 0.75 * mm});
            skCircle(sketch, "E33.43.1", {"center": v(-32.47, -26.86) * mm, "radius": 0.75 * mm});
            skCircle(sketch, "E33.43.2", {"center": v(-28.62, -23.67) * mm, "radius": 0.75 * mm});
            skCircle(sketch, "E33.43.3", {"center": v(-29.06, -19.22) * mm, "radius": 0.75 * mm});
            skCircle(sketch, "E33.44.0", {"center": v(-29.84, -26.35) * mm, "radius": 0.75 * mm});
            skCircle(sketch, "E33.44.1", {"center": v(-28.85, -30.72) * mm, "radius": 0.75 * mm});
            skCircle(sketch, "E33.44.2", {"center": v(-25.42, -27.07) * mm, "radius": 0.75 * mm});
            skCircle(sketch, "E33.44.3", {"center": v(-26.42, -22.7) * mm, "radius": 0.75 * mm});
            skCircle(sketch, "E33.45.0", {"center": v(-26.3, -29.89) * mm, "radius": 0.75 * mm});
            skCircle(sketch, "E33.45.1", {"center": v(-24.77, -34.1) * mm, "radius": 0.75 * mm});
            skCircle(sketch, "E33.45.2", {"center": v(-21.83, -30.05) * mm, "radius": 0.75 * mm});
            skCircle(sketch, "E33.45.3", {"center": v(-23.36, -25.84) * mm, "radius": 0.75 * mm});
            skCircle(sketch, "E33.46.0", {"center": v(-22.35, -32.95) * mm, "radius": 0.75 * mm});
            skCircle(sketch, "E33.46.1", {"center": v(-20.3, -36.93) * mm, "radius": 0.75 * mm});
            skCircle(sketch, "E33.46.2", {"center": v(-17.9, -32.55) * mm, "radius": 0.75 * mm});
            skCircle(sketch, "E33.46.3", {"center": v(-19.94, -28.57) * mm, "radius": 0.75 * mm});
            skCircle(sketch, "E33.47.0", {"center": v(-18.04, -35.49) * mm, "radius": 0.75 * mm});
            skCircle(sketch, "E33.47.1", {"center": v(-15.51, -39.18) * mm, "radius": 0.75 * mm});
            skCircle(sketch, "E33.47.2", {"center": v(-13.67, -34.53) * mm, "radius": 0.75 * mm});
            skCircle(sketch, "E33.47.3", {"center": v(-16.2, -30.84) * mm, "radius": 0.75 * mm});
            skCircle(sketch, "E33.48.0", {"center": v(-13.45, -37.47) * mm, "radius": 0.75 * mm});
            skCircle(sketch, "E33.48.1", {"center": v(-10.48, -40.81) * mm, "radius": 0.75 * mm});
            skCircle(sketch, "E33.48.2", {"center": v(-9.24, -35.97) * mm, "radius": 0.75 * mm});
            skCircle(sketch, "E33.48.3", {"center": v(-12.2, -32.63) * mm, "radius": 0.75 * mm});
            skCircle(sketch, "E33.49.0", {"center": v(-8.65, -38.86) * mm, "radius": 0.75 * mm});
            skCircle(sketch, "E33.49.1", {"center": v(-5.28, -41.8) * mm, "radius": 0.75 * mm});
            skCircle(sketch, "E33.49.2", {"center": v(-4.65, -36.85) * mm, "radius": 0.75 * mm});
            skCircle(sketch, "E33.49.3", {"center": v(-8.02, -33.9) * mm, "radius": 0.75 * mm});
            skPoint(sketch, "E33.center", {"position": v(0, 0) * mm});
            skSolve(sketch);
        }
        {
            var Q0;
            Q0 = qSketchRegion(id + "F12", true);
            extrude(context, id + "F13", {"entities" : qUnion([Q0]), "operationType" : NewBodyOperationType.REMOVE, "oppositeDirection" : true, "depth" : 25 * mm, "offsetDistance" : 25 * mm});
        }
        {
            var Q0;
            Q0=makeQuery(id+"F7.opExtrude","CAP_FACE",FACE,{"disambiguationData":[OSD([sQuery(id+"F6.wireOp",EDGE,"E11"),sQuery(id+"F6.wireOp",EDGE,"E12"),sQuery(id+"F6.wireOp",EDGE,"E13"),sQuery(id+"F6.wireOp",EDGE,"E14")])],"isStart":false});
            var sketch = newSketch(context, id + "F14", { "sketchPlane" : qUnion([Q0])});
            skLineSegment(sketch, "E34", {"start": v(-5.14, 14) * mm, "end": v(5.14, 14) * mm});
            skLineSegment(sketch, "E35", {"start": v(5.14, 14) * mm, "end": v(8.33, 0) * mm});
            skLineSegment(sketch, "E36", {"start": v(8.33, 0) * mm, "end": v(5.25, 0) * mm});
            skLineSegment(sketch, "E37", {"start": v(5.25, 0) * mm, "end": v(2.75, 11) * mm});
            skLineSegment(sketch, "E38", {"start": v(2.75, 11) * mm, "end": v(-2.75, 11) * mm});
            skLineSegment(sketch, "E39", {"start": v(-2.75, 11) * mm, "end": v(-5.25, 0) * mm});
            skLineSegment(sketch, "E40", {"start": v(-5.25, 0) * mm, "end": v(-8.33, 0) * mm});
            skLineSegment(sketch, "E41", {"start": v(-8.33, 0) * mm, "end": v(-5.14, 14) * mm});
            skSolve(sketch);
        }
        {
            var Q0;
            Q0=makeQuery(id+"F14.imprint","IMPRINT",FACE,{"disambiguationData":[TD([[makeQuery(id+"F14.imprint","IMPRINT",EDGE,{"derivedFrom":sQuery(id+"F14.wireOp",EDGE,"E34")}),-1.0]])]});
            extrude(context, id + "F15", {"entities" : qUnion([Q0]), "operationType" : NewBodyOperationType.ADD, "oppositeDirection" : true, "depth" : 7.1 * mm, "offsetDistance" : 25 * mm});
        }
    });
